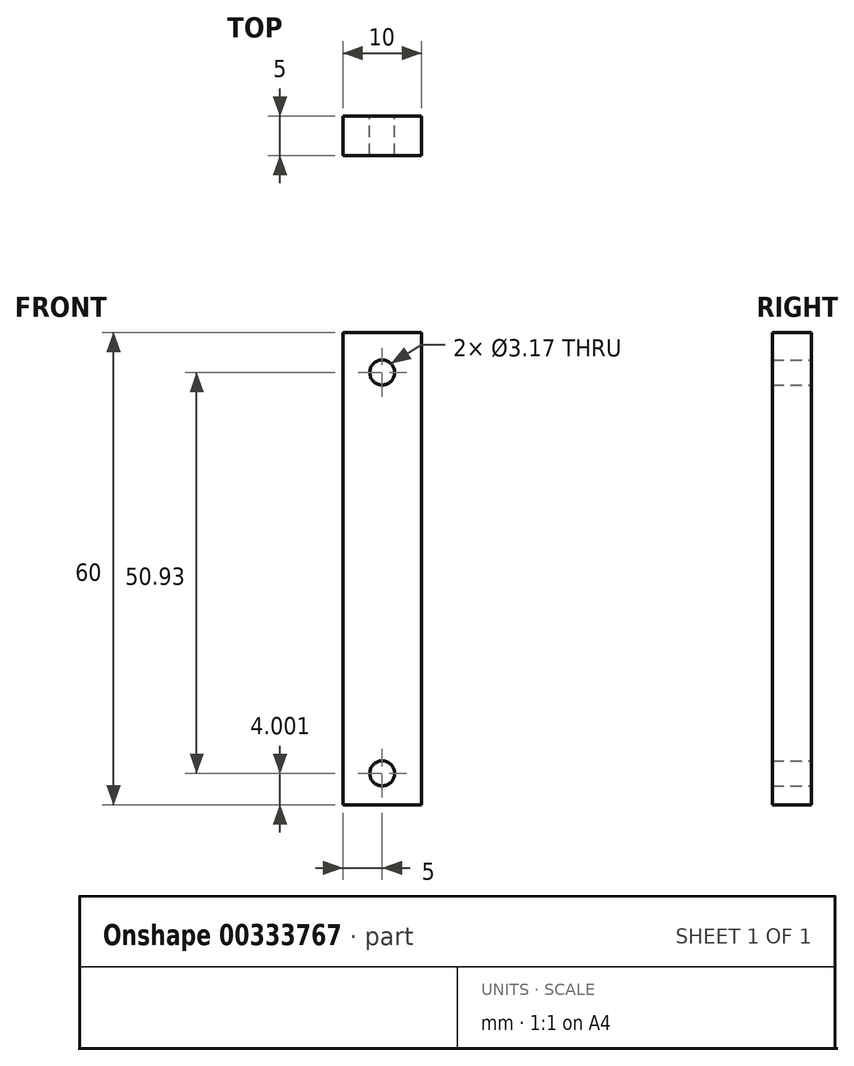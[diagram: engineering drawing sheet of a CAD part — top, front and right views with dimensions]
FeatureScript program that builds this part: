
annotation { "Feature Type Name" : "Feature", "Feature Type Description" : "" }
export const myFeature = defineFeature(function(context is Context, id is Id, definition is map)
    precondition{}
    {
        {
            var Q0;
            Q0=qCreatedBy(makeId("Front.planeOp"),FACE);
            var sketch = newSketch(context, id + "F0", { "sketchPlane" : qUnion([Q0])});
            skLineSegment(sketch, "E0.bottom", {"start": v(0, 45.22) * mm, "end": v(10, 45.22) * mm});
            skLineSegment(sketch, "E0.top", {"start": v(0, -14.78) * mm, "end": v(10, -14.78) * mm});
            skLineSegment(sketch, "E0.left", {"start": v(0, 45.22) * mm, "end": v(0, -14.78) * mm});
            skLineSegment(sketch, "E0.right", {"start": v(10, 45.22) * mm, "end": v(10, -14.78) * mm});
            skCircle(sketch, "E1", {"center": v(5, 40.15) * mm, "radius": 1.59 * mm});
            skCircle(sketch, "E2", {"center": v(5, -10.78) * mm, "radius": 1.59 * mm});
            skSolve(sketch);
        }
        {
            var Q0;
            Q0=qSketchRegion(id+"F0",true);
            extrude(context, id + "F1", {"entities" : qUnion([Q0]), "depth" : 5 * mm});
        }
    });
